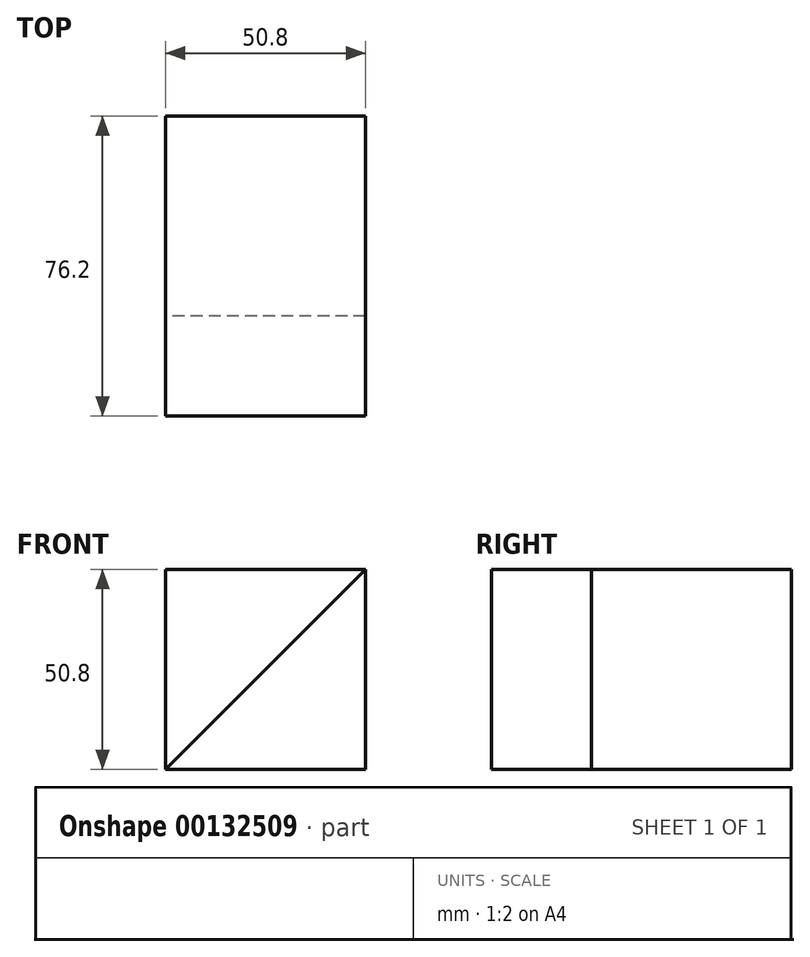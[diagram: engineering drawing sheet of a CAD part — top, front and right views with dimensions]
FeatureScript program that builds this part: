
annotation { "Feature Type Name" : "Feature", "Feature Type Description" : "" }
export const myFeature = defineFeature(function(context is Context, id is Id, definition is map)
    precondition{}
    {
        {
            var Q0;
            Q0=qCreatedBy(makeId("Front.planeOp"),FACE);
            var sketch = newSketch(context, id + "F0", { "sketchPlane" : qUnion([Q0])});
            skLineSegment(sketch, "E0.bottom", {"start": v(0, 0) * mm, "end": v(50.8, 0) * mm});
            skLineSegment(sketch, "E0.top", {"start": v(0, 50.8) * mm, "end": v(50.8, 50.8) * mm});
            skLineSegment(sketch, "E0.left", {"start": v(0, 0) * mm, "end": v(0, 50.8) * mm});
            skLineSegment(sketch, "E0.right", {"start": v(50.8, 0) * mm, "end": v(50.8, 50.8) * mm});
            skSolve(sketch);
        }
        {
            var Q0;
            Q0=makeQuery(id+"F0.imprint","IMPRINT",FACE,{"disambiguationData":[TD([[makeQuery(id+"F0.imprint","IMPRINT",EDGE,{"derivedFrom":sQuery(id+"F0.wireOp",EDGE,"E0.bottom")}),1.0]])]});
            extrude(context, id + "F1", {"entities" : qUnion([Q0]), "depth" : 50.8 * mm});
        }
        {
            var Q0;
            Q0=makeQuery(id+"F1.opExtrude","CAP_FACE",FACE,{"disambiguationData":[OSD([sQuery(id+"F0.wireOp",EDGE,"E0.bottom"),sQuery(id+"F0.wireOp",EDGE,"E0.top"),sQuery(id+"F0.wireOp",EDGE,"E0.left"),sQuery(id+"F0.wireOp",EDGE,"E0.right")])],"isStart":false});
            var sketch = newSketch(context, id + "F2", { "sketchPlane" : qUnion([Q0])});
            skLineSegment(sketch, "E1", {"start": v(50.8, 50.8) * mm, "end": v(0, 0) * mm});
            skSolve(sketch);
        }
        {
            var Q0;
            Q0=makeQuery(id+"F2.imprint","IMPRINT",FACE,{"disambiguationData":[TD([[makeQuery(id+"F2.imprint","IMPRINT",EDGE,{"derivedFrom":sQuery(id+"F2.wireOp",EDGE,"E1")}),-1.0]])]});
            extrude(context, id + "F3", {"entities" : qUnion([Q0]), "operationType" : NewBodyOperationType.ADD, "depth" : 25.4 * mm});
        }
    });
